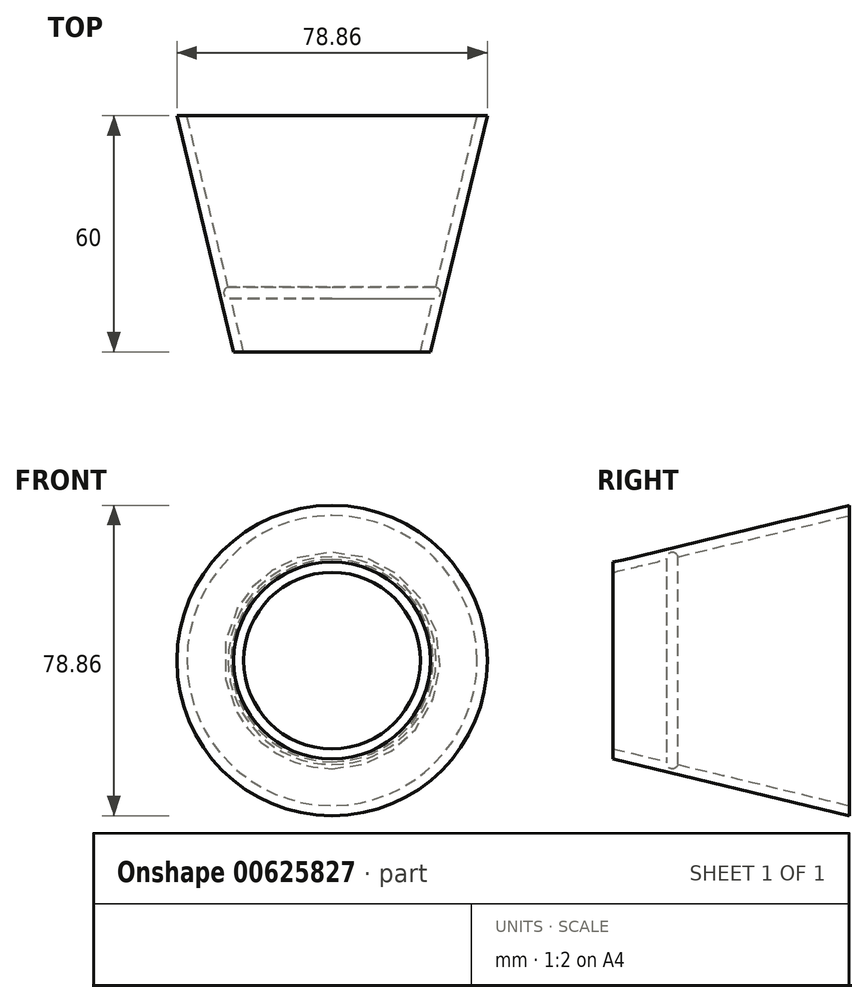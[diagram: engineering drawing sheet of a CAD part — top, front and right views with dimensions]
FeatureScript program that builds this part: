
annotation { "Feature Type Name" : "Feature", "Feature Type Description" : "" }
export const myFeature = defineFeature(function(context is Context, id is Id, definition is map)
    precondition{}
    {
        {
            var Q0;
            Q0=qCreatedBy(makeId("Top.planeOp"),FACE);
            var sketch = newSketch(context, id + "F0", { "sketchPlane" : qUnion([Q0])});
            skLineSegment(sketch, "E0", {"start": v(-25, 0) * mm, "end": v(-39.43, 60) * mm});
            skLineSegment(sketch, "E1", {"start": v(-39.43, 60) * mm, "end": v(0, 60) * mm});
            skLineSegment(sketch, "E2", {"start": v(0, 60) * mm, "end": v(0, 0) * mm});
            skLineSegment(sketch, "E3", {"start": v(0, 0) * mm, "end": v(-25, 0) * mm});
            skSolve(sketch);
        }
        {
            var Q0;
            Q0 = qSketchRegion(id + "F0", true);
            var Q1;
            Q1=sQuery(id+"F0.wireOp",EDGE,"E2");
            revolve(context, id + "F1", {"entities" : qUnion([Q0]), "axis" : qUnion([Q1]), "revolveType" : RevolveType.FULL});
        }
        {
            var Q0;
            Q0=makeQuery(id+"F1.opRevolve","SWEPT_FACE",FACE,{"disambiguationData":[OSD([sQuery(id+"F0.wireOp",EDGE,"E1")])]});
            var Q1;
            Q1=makeQuery(id+"F1.opRevolve","SWEPT_FACE",FACE,{"disambiguationData":[OSD([sQuery(id+"F0.wireOp",EDGE,"E3")])]});
            shell(context, id + "F2", {"entities" : qUnion([Q0, Q1]), "thickness" : 2.5 * mm});
        }
        {
            var Q0;
            Q0=qCreatedBy(makeId("Right.planeOp"),FACE);
            var sketch = newSketch(context, id + "F3", { "sketchPlane" : qUnion([Q0])});
            skCircle(sketch, "E4", {"center": v(15, 26) * mm, "radius": 1.5 * mm});
            skLineSegment(sketch, "E5", {"start": v(0, 0) * mm, "end": v(38.6, 0) * mm, "construction": true});
            skSolve(sketch);
        }
        {
            var Q0;
            Q0 = qSketchRegion(id + "F3", true);
            var Q1;
            Q1=sQuery(id+"F3.wireOp",EDGE,"E5");
            revolve(context, id + "F4", {"operationType" : NewBodyOperationType.REMOVE, "entities" : qUnion([Q0]), "axis" : qUnion([Q1]), "revolveType" : RevolveType.FULL});
        }
    });
